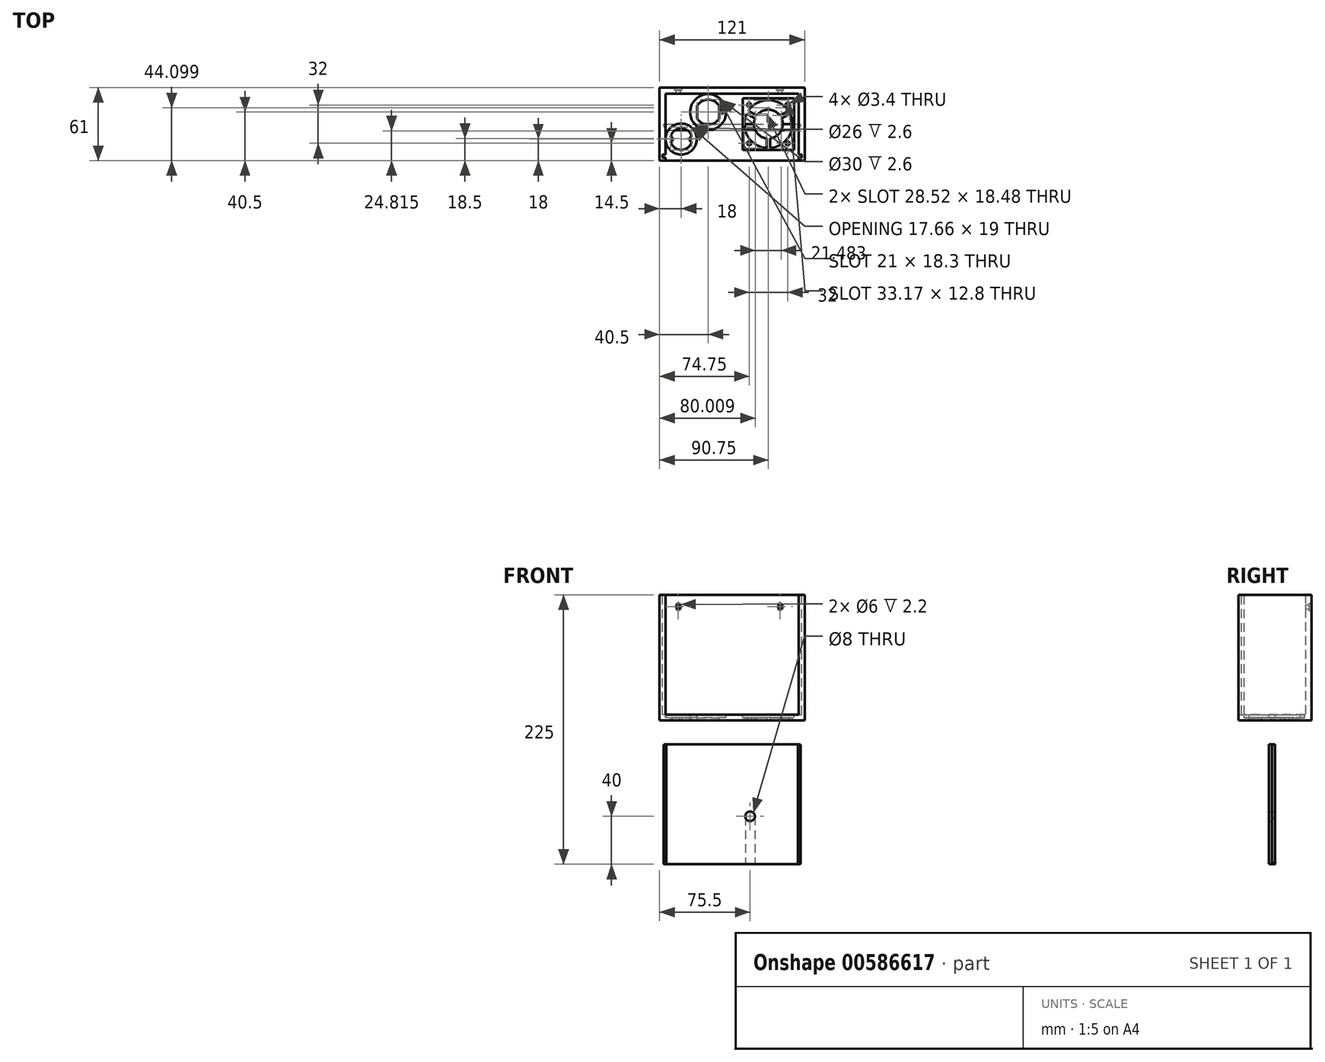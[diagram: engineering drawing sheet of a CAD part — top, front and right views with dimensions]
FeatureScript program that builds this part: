
annotation { "Feature Type Name" : "Feature", "Feature Type Description" : "" }
export const myFeature = defineFeature(function(context is Context, id is Id, definition is map)
    precondition{}
    {
        {
            var Q0;
            Q0=qCreatedBy(makeId("Top.planeOp"),FACE);
            var sketch = newSketch(context, id + "F0", { "sketchPlane" : qUnion([Q0])});
            skLineSegment(sketch, "E0.bottom", {"start": v(-55.5, -25.5) * mm, "end": v(55.5, -25.5) * mm});
            skLineSegment(sketch, "E0.top", {"start": v(-55.5, 25.5) * mm, "end": v(55.5, 25.5) * mm});
            skLineSegment(sketch, "E0.left", {"start": v(-55.5, -25.5) * mm, "end": v(-55.5, 25.5) * mm});
            skLineSegment(sketch, "E0.right", {"start": v(55.5, -25.5) * mm, "end": v(55.5, 25.5) * mm});
            skPoint(sketch, "E0.middle", {"position": v(0, 0) * mm});
            skLineSegment(sketch, "E1.0", {"start": v(60.5, -30.5) * mm, "end": v(60.5, 30.5) * mm});
            skLineSegment(sketch, "E1.1", {"start": v(-60.5, -30.5) * mm, "end": v(60.5, -30.5) * mm});
            skLineSegment(sketch, "E1.2", {"start": v(-60.5, -30.5) * mm, "end": v(-60.5, 30.5) * mm});
            skLineSegment(sketch, "E1.3", {"start": v(-60.5, 30.5) * mm, "end": v(60.5, 30.5) * mm});
            skSolve(sketch);
        }
        {
            var Q0;
            Q0=makeQuery(id+"F0.imprint","IMPRINT",FACE,{"disambiguationData":[TD([[makeQuery(id+"F0.imprint","IMPRINT",EDGE,{"derivedFrom":sQuery(id+"F0.wireOp",EDGE,"E0.bottom")}),-1.0]])]});
            extrude(context, id + "F1", {"entities" : qUnion([Q0]), "depth" : 100 * mm, "offsetDistance" : 25 * mm});
        }
        {
            var Q0;
            Q0=qCreatedBy(makeId("Top.planeOp"),FACE);
            var sketch = newSketch(context, id + "F2", { "sketchPlane" : qUnion([Q0])});
            skLineSegment(sketch, "E2.bottom", {"start": v(60.5, -30.5) * mm, "end": v(-60.5, -30.5) * mm});
            skLineSegment(sketch, "E2.top", {"start": v(60.5, 30.5) * mm, "end": v(-60.5, 30.5) * mm});
            skLineSegment(sketch, "E2.left", {"start": v(60.5, -30.5) * mm, "end": v(60.5, 30.5) * mm});
            skLineSegment(sketch, "E2.right", {"start": v(-60.5, -30.5) * mm, "end": v(-60.5, 30.5) * mm});
            skPoint(sketch, "E2.middle", {"position": v(0, 0) * mm});
            skSolve(sketch);
        }
        {
            var Q0;
            Q0=makeQuery(id+"F2.imprint","IMPRINT",FACE,{"disambiguationData":[TD([[makeQuery(id+"F2.imprint","IMPRINT",EDGE,{"derivedFrom":sQuery(id+"F2.wireOp",EDGE,"E2.bottom")}),-1.0]])]});
            extrude(context, id + "F3", {"entities" : qUnion([Q0]), "operationType" : NewBodyOperationType.ADD, "oppositeDirection" : true, "depth" : 5 * mm, "offsetDistance" : 25 * mm});
        }
        {
            var Q0;
            Q0=qCreatedBy(makeId("Top.planeOp"),FACE);
            var sketch = newSketch(context, id + "F4", { "sketchPlane" : qUnion([Q0])});
            skArc(sketch, "E3", {"start": v(-33.67, -10.75) * mm, "mid": v(-36.41, -5.87) * mm, "end": v(-41.5, -3.56) * mm});
            skArc(sketch, "E4", {"start": v(-29.15, 4.85) * mm, "mid": v(-20, -0.5) * mm, "end": v(-10.85, 4.85) * mm});
            skLineSegment(sketch, "E5.top", {"start": v(-29.15, 15.15) * mm, "end": v(-10.85, 15.15) * mm, "construction": true});
            skLineSegment(sketch, "E5.left", {"start": v(-29.15, 4.85) * mm, "end": v(-29.15, 15.15) * mm});
            skLineSegment(sketch, "E5.right", {"start": v(-10.85, 4.85) * mm, "end": v(-10.85, 15.15) * mm});
            skArc(sketch, "E6.trimOffspring", {"start": v(-10.85, 15.15) * mm, "mid": v(-20, 20.5) * mm, "end": v(-29.15, 15.15) * mm});
            skLineSegment(sketch, "E7.bottom", {"start": v(-35.15, -14.25) * mm, "end": v(-49.85, -14.25) * mm, "construction": true});
            skLineSegment(sketch, "E7.top", {"start": v(-35.15, -10.75) * mm, "end": v(-49.85, -10.75) * mm, "construction": true});
            skLineSegment(sketch, "E7.left", {"start": v(-35.15, -14.25) * mm, "end": v(-35.15, -10.75) * mm});
            skLineSegment(sketch, "E7.right", {"start": v(-49.85, -14.25) * mm, "end": v(-49.85, -10.75) * mm});
            skLineSegment(sketch, "E8", {"start": v(-49.85, -14.25) * mm, "end": v(-51.33, -14.25) * mm});
            skLineSegment(sketch, "E9", {"start": v(-35.15, -10.75) * mm, "end": v(-33.67, -10.75) * mm});
            skLineSegment(sketch, "E10", {"start": v(-35.15, -14.25) * mm, "end": v(-33.67, -14.25) * mm});
            skLineSegment(sketch, "E11", {"start": v(-49.85, -10.75) * mm, "end": v(-51.33, -10.75) * mm});
            skArc(sketch, "E12.trimOffspring", {"start": v(-51.33, -14.25) * mm, "mid": v(-42.5, -21.5) * mm, "end": v(-33.67, -14.25) * mm});
            skArc(sketch, "E13", {"start": v(-41.5, -3.56) * mm, "mid": v(-42.5, -2.5) * mm, "end": v(-43.5, -3.56) * mm});
            skArc(sketch, "E14.trimOffspring", {"start": v(-43.5, -3.56) * mm, "mid": v(-48.59, -5.87) * mm, "end": v(-51.33, -10.75) * mm});
            skSolve(sketch);
        }
        {
            var Q0;
            Q0=makeQuery(id+"F4.imprint","IMPRINT",FACE,{"disambiguationData":[TD([[makeQuery(id+"F4.imprint","IMPRINT",EDGE,{"derivedFrom":sQuery(id+"F4.wireOp",EDGE,"E3")}),1.0]])]});
            var Q1;
            Q1=makeQuery(id+"F4.imprint","IMPRINT",FACE,{"disambiguationData":[TD([[makeQuery(id+"F4.imprint","IMPRINT",EDGE,{"derivedFrom":sQuery(id+"F4.wireOp",EDGE,"E4")}),1.0]])]});
            var Q2;
            Q2=sQuery(id+"F4.wireOp",EDGE,"E3");
            extrude(context, id + "F5", {"entities" : qUnion([Q0, Q1]), "operationType" : NewBodyOperationType.REMOVE, "surfaceEntities" : qUnion([Q2]), "oppositeDirection" : true, "depth" : 25 * mm, "offsetDistance" : 25 * mm});
        }
        {
            var Q0;
            Q0=makeQuery(id+"F3.boolean.opBoolean","MERGE",FACE,{"derivedFrom":[makeQuery(id+"F1.opExtrude","SWEPT_FACE",FACE,{"disambiguationData":[OSD([sQuery(id+"F0.wireOp",EDGE,"E1.3")])]}),makeQuery(id+"F3.opExtrude","SWEPT_FACE",FACE,{"disambiguationData":[OSD([sQuery(id+"F2.wireOp",EDGE,"E2.top")])]})]});
            cPlane(context, id + "F6", {"entities" : qUnion([Q0]), "cplaneType" : CPlaneType.OFFSET, "offset" : 0 * mm, "width" : 150 * mm, "height" : 150 * mm});
        }
        {
            var Q0;
            Q0=qCreatedBy(id+"F6.planeOp",FACE);
            var sketch = newSketch(context, id + "F7", { "sketchPlane" : qUnion([Q0])});
            skCircle(sketch, "E15", {"center": v(45, 90) * mm, "radius": 1.7 * mm});
            skLineSegment(sketch, "E16.bottom", {"start": v(-55.5, 0) * mm, "end": v(55.5, 0) * mm});
            skLineSegment(sketch, "E16.top", {"start": v(-55.5, 100) * mm, "end": v(55.5, 100) * mm});
            skLineSegment(sketch, "E16.left", {"start": v(-55.5, 0) * mm, "end": v(-55.5, 100) * mm});
            skLineSegment(sketch, "E16.right", {"start": v(55.5, 0) * mm, "end": v(55.5, 100) * mm});
            skCircle(sketch, "E17", {"center": v(-40, 90) * mm, "radius": 1.7 * mm});
            skSolve(sketch);
        }
        {
            var Q0;
            Q0=makeQuery(id+"F7.imprint","IMPRINT",FACE,{"disambiguationData":[TD([[makeQuery(id+"F7.imprint","IMPRINT",EDGE,{"derivedFrom":sQuery(id+"F7.wireOp",EDGE,"E17")}),1.0]])]});
            var Q1;
            Q1=makeQuery(id+"F7.imprint","IMPRINT",FACE,{"disambiguationData":[TD([[makeQuery(id+"F7.imprint","IMPRINT",EDGE,{"derivedFrom":sQuery(id+"F7.wireOp",EDGE,"E15")}),1.0]])]});
            extrude(context, id + "F8", {"entities" : qUnion([Q0, Q1]), "operationType" : NewBodyOperationType.REMOVE, "oppositeDirection" : true, "depth" : 25 * mm, "offsetDistance" : 25 * mm});
        }
        {
            var Q0;
            Q0=makeQuery(id+"F3.opExtrude","CAP_FACE",FACE,{"disambiguationData":[OSD([sQuery(id+"F2.wireOp",EDGE,"E2.bottom"),sQuery(id+"F2.wireOp",EDGE,"E2.top"),sQuery(id+"F2.wireOp",EDGE,"E2.left"),sQuery(id+"F2.wireOp",EDGE,"E2.right")])],"isStart":false});
            cPlane(context, id + "F9", {"entities" : qUnion([Q0]), "cplaneType" : CPlaneType.OFFSET, "offset" : 0 * mm, "width" : 150 * mm, "height" : 150 * mm});
        }
        {
            var Q0;
            Q0=qCreatedBy(id+"F9.planeOp",FACE);
            var sketch = newSketch(context, id + "F10", { "sketchPlane" : qUnion([Q0])});
            skLineSegment(sketch, "E18.bottom", {"start": v(46.25, 16) * mm, "end": v(14.25, 16) * mm, "construction": true});
            skLineSegment(sketch, "E18.top", {"start": v(46.25, -16) * mm, "end": v(14.25, -16) * mm, "construction": true});
            skLineSegment(sketch, "E18.left", {"start": v(46.25, 16) * mm, "end": v(46.25, -16) * mm, "construction": true});
            skLineSegment(sketch, "E18.right", {"start": v(14.25, 16) * mm, "end": v(14.25, -16) * mm, "construction": true});
            skPoint(sketch, "E18.middle", {"position": v(30.25, 0) * mm});
            skLineSegment(sketch, "E19", {"start": v(0, 0) * mm, "end": v(60.5, 0) * mm, "construction": true});
            skCircle(sketch, "E20", {"center": v(14.25, 16) * mm, "radius": 1.7 * mm});
            skCircle(sketch, "E21", {"center": v(46.25, 16) * mm, "radius": 1.7 * mm});
            skCircle(sketch, "E22", {"center": v(46.25, -16) * mm, "radius": 1.7 * mm});
            skCircle(sketch, "E23", {"center": v(14.25, -16) * mm, "radius": 1.7 * mm});
            skLineSegment(sketch, "E24.bottom", {"start": v(30.25, 20) * mm, "end": v(50.25, 20) * mm, "construction": true});
            skLineSegment(sketch, "E24.top", {"start": v(10.25, -20) * mm, "end": v(50.25, -20) * mm, "construction": true});
            skLineSegment(sketch, "E24.left", {"start": v(10.25, 20) * mm, "end": v(10.25, -20) * mm, "construction": true});
            skLineSegment(sketch, "E24.right", {"start": v(50.25, 20) * mm, "end": v(50.25, -20) * mm, "construction": true});
            skArc(sketch, "E25", {"start": v(28.75, 19.94) * mm, "mid": v(12.96, 10.05) * mm, "end": v(12.18, -8.57) * mm});
            skArc(sketch, "E26", {"start": v(28.75, 11.9) * mm, "mid": v(19.87, 6.03) * mm, "end": v(19.16, -4.6) * mm});
            skLineSegment(sketch, "E27", {"start": v(30.25, 0) * mm, "end": v(30.25, 20) * mm, "construction": true});
            skLineSegment(sketch, "E28", {"start": v(30.25, 0) * mm, "end": v(47.63, -9.9) * mm, "construction": true});
            skLineSegment(sketch, "E29.MirrorCS", {"start": v(30.25, 0) * mm, "end": v(12.87, -9.9) * mm, "construction": true});
            skLineSegment(sketch, "E30.0", {"start": v(31.75, 11.9) * mm, "end": v(31.75, 19.94) * mm});
            skLineSegment(sketch, "E30.1", {"start": v(41.34, -4.6) * mm, "end": v(48.32, -8.57) * mm});
            skLineSegment(sketch, "E31.0", {"start": v(39.85, -7.2) * mm, "end": v(46.83, -11.18) * mm});
            skLineSegment(sketch, "E31.1", {"start": v(20.65, -7.2) * mm, "end": v(13.67, -11.18) * mm});
            skLineSegment(sketch, "E32.1", {"start": v(28.75, 11.9) * mm, "end": v(28.75, 19.94) * mm});
            skPoint(sketch, "E33.orphan", {"position": v(10.25, -11.4) * mm});
            skPoint(sketch, "E34.orphan", {"position": v(50.25, -11.4) * mm});
            skLineSegment(sketch, "E35.trimOffspring", {"start": v(19.16, -4.6) * mm, "end": v(12.18, -8.57) * mm});
            skArc(sketch, "E36.trimOffspring", {"start": v(41.34, -4.6) * mm, "mid": v(40.63, 6.03) * mm, "end": v(31.75, 11.9) * mm});
            skArc(sketch, "E37.trimOffspring", {"start": v(48.32, -8.57) * mm, "mid": v(47.54, 10.05) * mm, "end": v(31.75, 19.94) * mm});
            skArc(sketch, "E38.trimOffspring", {"start": v(20.65, -7.2) * mm, "mid": v(30.25, -12) * mm, "end": v(39.85, -7.2) * mm});
            skArc(sketch, "E39.trimOffspring", {"start": v(13.67, -11.18) * mm, "mid": v(30.25, -20) * mm, "end": v(46.83, -11.18) * mm});
            skSolve(sketch);
        }
        {
            var Q0;
            Q0=makeQuery(id+"F10.imprint","IMPRINT",FACE,{"disambiguationData":[TD([[makeQuery(id+"F10.imprint","IMPRINT",EDGE,{"derivedFrom":sQuery(id+"F10.wireOp",EDGE,"E20")}),1.0]])]});
            var Q1;
            Q1=makeQuery(id+"F10.imprint","IMPRINT",FACE,{"disambiguationData":[TD([[makeQuery(id+"F10.imprint","IMPRINT",EDGE,{"derivedFrom":sQuery(id+"F10.wireOp",EDGE,"E25")}),1.0]])]});
            var Q2;
            Q2=makeQuery(id+"F10.imprint","IMPRINT",FACE,{"disambiguationData":[TD([[makeQuery(id+"F10.imprint","IMPRINT",EDGE,{"derivedFrom":sQuery(id+"F10.wireOp",EDGE,"E30.0")}),-1.0]])]});
            var Q3;
            Q3=makeQuery(id+"F10.imprint","IMPRINT",FACE,{"disambiguationData":[TD([[makeQuery(id+"F10.imprint","IMPRINT",EDGE,{"derivedFrom":sQuery(id+"F10.wireOp",EDGE,"E21")}),1.0]])]});
            var Q4;
            Q4=makeQuery(id+"F10.imprint","IMPRINT",FACE,{"disambiguationData":[TD([[makeQuery(id+"F10.imprint","IMPRINT",EDGE,{"derivedFrom":sQuery(id+"F10.wireOp",EDGE,"E31.0")}),-1.0]])]});
            var Q5;
            Q5=makeQuery(id+"F10.imprint","IMPRINT",FACE,{"disambiguationData":[TD([[makeQuery(id+"F10.imprint","IMPRINT",EDGE,{"derivedFrom":sQuery(id+"F10.wireOp",EDGE,"E23")}),1.0]])]});
            var Q6;
            Q6=makeQuery(id+"F10.imprint","IMPRINT",FACE,{"disambiguationData":[TD([[makeQuery(id+"F10.imprint","IMPRINT",EDGE,{"derivedFrom":sQuery(id+"F10.wireOp",EDGE,"E22")}),1.0]])]});
            extrude(context, id + "F11", {"entities" : qUnion([Q0, Q1, Q2, Q3, Q4, Q5, Q6]), "operationType" : NewBodyOperationType.REMOVE, "oppositeDirection" : true, "depth" : 25 * mm, "offsetDistance" : 25 * mm});
        }
        {
            var Q0;
            Q0=qCreatedBy(id+"F6.planeOp",FACE);
            var sketch = newSketch(context, id + "F12", { "sketchPlane" : qUnion([Q0])});
            skCircle(sketch, "E40", {"center": v(-40, 90) * mm, "radius": 3 * mm});
            skCircle(sketch, "E41", {"center": v(45, 90) * mm, "radius": 3 * mm});
            skSolve(sketch);
        }
        {
            var Q0;
            Q0=makeQuery(id+"F12.imprint","IMPRINT",FACE,{"disambiguationData":[TD([[makeQuery(id+"F12.imprint","IMPRINT",EDGE,{"derivedFrom":sQuery(id+"F12.wireOp",EDGE,"E40")}),1.0]])]});
            var Q1;
            Q1=makeQuery(id+"F12.imprint","IMPRINT",FACE,{"disambiguationData":[TD([[makeQuery(id+"F12.imprint","IMPRINT",EDGE,{"derivedFrom":sQuery(id+"F12.wireOp",EDGE,"E41")}),1.0]])]});
            extrude(context, id + "F13", {"entities" : qUnion([Q0, Q1]), "operationType" : NewBodyOperationType.REMOVE, "oppositeDirection" : true, "depth" : 2.2 * mm, "offsetDistance" : 25 * mm});
        }
        {
            var Q0;
            Q0=qCreatedBy(makeId("Top.planeOp"),FACE);
            var sketch = newSketch(context, id + "F14", { "sketchPlane" : qUnion([Q0])});
            skCircle(sketch, "E42", {"center": v(-20, 10) * mm, "radius": 15 * mm});
            skCircle(sketch, "E43", {"center": v(-42.5, -12.5) * mm, "radius": 13 * mm});
            skLineSegment(sketch, "E44.bottom", {"start": v(8.75, -21.5) * mm, "end": v(51.75, -21.5) * mm});
            skLineSegment(sketch, "E44.top", {"start": v(8.75, 21.5) * mm, "end": v(51.75, 21.5) * mm});
            skLineSegment(sketch, "E44.left", {"start": v(8.75, -21.5) * mm, "end": v(8.75, 21.5) * mm});
            skLineSegment(sketch, "E44.right", {"start": v(51.75, -21.5) * mm, "end": v(51.75, 21.5) * mm});
            skPoint(sketch, "E44.middle", {"position": v(30.25, 0) * mm});
            skSolve(sketch);
        }
        {
            var Q0;
            Q0=makeQuery(id+"F14.imprint","IMPRINT",FACE,{"disambiguationData":[TD([[makeQuery(id+"F14.imprint","IMPRINT",EDGE,{"derivedFrom":sQuery(id+"F14.wireOp",EDGE,"E42")}),1.0]])]});
            var Q1;
            Q1=makeQuery(id+"F14.imprint","IMPRINT",FACE,{"disambiguationData":[TD([[makeQuery(id+"F14.imprint","IMPRINT",EDGE,{"derivedFrom":sQuery(id+"F14.wireOp",EDGE,"E43")}),1.0]])]});
            var Q2;
            Q2=makeQuery(id+"F14.imprint","IMPRINT",FACE,{"disambiguationData":[TD([[makeQuery(id+"F14.imprint","IMPRINT",EDGE,{"derivedFrom":sQuery(id+"F14.wireOp",EDGE,"E44.bottom")}),1.0]])]});
            extrude(context, id + "F15", {"entities" : qUnion([Q0, Q1, Q2]), "operationType" : NewBodyOperationType.REMOVE, "oppositeDirection" : true, "depth" : 2.6 * mm, "offsetDistance" : 25 * mm});
        }
        {
            var Q0;
            Q0=makeQuery(id+"F3.boolean.opBoolean","MERGE",FACE,{"derivedFrom":[makeQuery(id+"F1.opExtrude","SWEPT_FACE",FACE,{"disambiguationData":[OSD([sQuery(id+"F0.wireOp",EDGE,"E1.1")])]}),makeQuery(id+"F3.opExtrude","SWEPT_FACE",FACE,{"disambiguationData":[OSD([sQuery(id+"F2.wireOp",EDGE,"E2.bottom")])]})]});
            cPlane(context, id + "F16", {"entities" : qUnion([Q0]), "cplaneType" : CPlaneType.OFFSET, "offset" : 0 * mm, "width" : 150 * mm, "height" : 150 * mm});
        }
        {
            var Q0;
            Q0=qCreatedBy(id+"F16.planeOp",FACE);
            var sketch = newSketch(context, id + "F17", { "sketchPlane" : qUnion([Q0])});
            skLineSegment(sketch, "E45.bottom", {"start": v(-55.5, 100) * mm, "end": v(55.5, 100) * mm});
            skLineSegment(sketch, "E45.top", {"start": v(-55.5, 0) * mm, "end": v(55.5, 0) * mm});
            skLineSegment(sketch, "E45.left", {"start": v(-55.5, 100) * mm, "end": v(-55.5, 0) * mm});
            skLineSegment(sketch, "E45.right", {"start": v(55.5, 100) * mm, "end": v(55.5, 0) * mm});
            skSolve(sketch);
        }
        {
            var Q0;
            Q0 = qSketchRegion(id + "F17", true);
            extrude(context, id + "F18", {"entities" : qUnion([Q0]), "operationType" : NewBodyOperationType.REMOVE, "oppositeDirection" : true, "depth" : 25 * mm, "offsetDistance" : 25 * mm});
        }
        {
            var Q0;
            Q0=makeQuery(id+"F1.opExtrude","CAP_FACE",FACE,{"disambiguationData":[OSD([sQuery(id+"F0.wireOp",EDGE,"E0.bottom"),sQuery(id+"F0.wireOp",EDGE,"E0.top"),sQuery(id+"F0.wireOp",EDGE,"E0.left"),sQuery(id+"F0.wireOp",EDGE,"E0.right"),sQuery(id+"F0.wireOp",EDGE,"E1.0"),sQuery(id+"F0.wireOp",EDGE,"E1.1"),sQuery(id+"F0.wireOp",EDGE,"E1.2"),sQuery(id+"F0.wireOp",EDGE,"E1.3")])],"isStart":false});
            cPlane(context, id + "F19", {"entities" : qUnion([Q0]), "cplaneType" : CPlaneType.OFFSET, "offset" : 0 * mm, "width" : 150 * mm, "height" : 150 * mm});
        }
        {
            var Q0;
            Q0=qCreatedBy(id+"F19.planeOp",FACE);
            var sketch = newSketch(context, id + "F20", { "sketchPlane" : qUnion([Q0])});
            skLineSegment(sketch, "E46.bottom", {"start": v(55.5, -28) * mm, "end": v(58, -28) * mm});
            skLineSegment(sketch, "E46.top", {"start": v(55.5, -25.5) * mm, "end": v(58, -25.5) * mm});
            skLineSegment(sketch, "E46.left", {"start": v(55.5, -28) * mm, "end": v(55.5, -25.5) * mm});
            skLineSegment(sketch, "E46.right", {"start": v(58, -28) * mm, "end": v(58, -25.5) * mm});
            skLineSegment(sketch, "E47.MirrorCS", {"start": v(-55.5, -25.5) * mm, "end": v(-58, -25.5) * mm});
            skLineSegment(sketch, "E48.MirrorCS", {"start": v(-58, -28) * mm, "end": v(-58, -25.5) * mm});
            skLineSegment(sketch, "E49.MirrorCS", {"start": v(-55.5, -28) * mm, "end": v(-58, -28) * mm});
            skLineSegment(sketch, "E50.MirrorCS", {"start": v(-55.5, -28) * mm, "end": v(-55.5, -25.5) * mm});
            skSolve(sketch);
        }
        {
            var Q0;
            Q0=makeQuery(id+"F20.imprint","IMPRINT",FACE,{"disambiguationData":[TD([[makeQuery(id+"F20.imprint","IMPRINT",EDGE,{"derivedFrom":sQuery(id+"F20.wireOp",EDGE,"E47.MirrorCS")}),1.0]])]});
            var Q1;
            Q1=makeQuery(id+"F20.imprint","IMPRINT",FACE,{"disambiguationData":[TD([[makeQuery(id+"F20.imprint","IMPRINT",EDGE,{"derivedFrom":sQuery(id+"F20.wireOp",EDGE,"E46.bottom")}),1.0]])]});
            extrude(context, id + "F21", {"entities" : qUnion([Q0, Q1]), "operationType" : NewBodyOperationType.REMOVE, "oppositeDirection" : true, "depth" : 100 * mm, "offsetDistance" : 25 * mm});
        }
        {
            var Q0;
            Q0=qCreatedBy(makeId("Front.planeOp"),FACE);
            var sketch = newSketch(context, id + "F22", { "sketchPlane" : qUnion([Q0])});
            skLineSegment(sketch, "E51.bottom", {"start": v(-55, -25) * mm, "end": v(55, -25) * mm});
            skLineSegment(sketch, "E51.top", {"start": v(-55, -125) * mm, "end": v(55, -125) * mm});
            skLineSegment(sketch, "E51.left", {"start": v(-55, -25) * mm, "end": v(-55, -125) * mm});
            skLineSegment(sketch, "E51.right", {"start": v(55, -25) * mm, "end": v(55, -125) * mm});
            skPoint(sketch, "E51.middle", {"position": v(0, -75) * mm});
            skLineSegment(sketch, "E52", {"start": v(0, 0) * mm, "end": v(0, -150) * mm, "construction": true});
            skCircle(sketch, "E53", {"center": v(15, -85) * mm, "radius": 4 * mm});
            skSolve(sketch);
        }
        {
            var Q0;
            Q0=makeQuery(id+"F22.imprint","IMPRINT",FACE,{"disambiguationData":[TD([[makeQuery(id+"F22.imprint","IMPRINT",EDGE,{"derivedFrom":sQuery(id+"F22.wireOp",EDGE,"E51.bottom")}),-1.0]])]});
            extrude(context, id + "F23", {"entities" : qUnion([Q0]), "depth" : 5 * mm, "offsetDistance" : 25 * mm});
        }
        {
            var Q0;
            Q0=makeQuery(id+"F23.opExtrude","SWEPT_FACE",FACE,{"disambiguationData":[OSD([sQuery(id+"F22.wireOp",EDGE,"E51.top")])]});
            var sketch = newSketch(context, id + "F24", { "sketchPlane" : qUnion([Q0])});
            skLineSegment(sketch, "E54.bottom", {"start": v(55, 0) * mm, "end": v(57.3, 0) * mm});
            skLineSegment(sketch, "E54.top", {"start": v(55, 2.3) * mm, "end": v(57.3, 2.3) * mm});
            skLineSegment(sketch, "E54.left", {"start": v(55, 0) * mm, "end": v(55, 2.3) * mm});
            skLineSegment(sketch, "E54.right", {"start": v(57.3, 0) * mm, "end": v(57.3, 2.3) * mm});
            skLineSegment(sketch, "E55.MirrorCS", {"start": v(-55, 0) * mm, "end": v(-55, 2.3) * mm});
            skLineSegment(sketch, "E56.MirrorCS", {"start": v(-55, 2.3) * mm, "end": v(-57.3, 2.3) * mm});
            skLineSegment(sketch, "E57.MirrorCS", {"start": v(-57.3, 0) * mm, "end": v(-57.3, 2.3) * mm});
            skLineSegment(sketch, "E58.MirrorCS", {"start": v(-55, 0) * mm, "end": v(-57.3, 0) * mm});
            skSolve(sketch);
        }
        {
            var Q0;
            Q0=makeQuery(id+"F24.imprint","IMPRINT",FACE,{"disambiguationData":[TD([[makeQuery(id+"F24.imprint","IMPRINT",EDGE,{"derivedFrom":sQuery(id+"F24.wireOp",EDGE,"E54.bottom")}),1.0]])]});
            var Q1;
            Q1=makeQuery(id+"F24.imprint","IMPRINT",FACE,{"disambiguationData":[TD([[makeQuery(id+"F24.imprint","IMPRINT",EDGE,{"derivedFrom":sQuery(id+"F24.wireOp",EDGE,"E55.MirrorCS")}),-1.0]])]});
            extrude(context, id + "F25", {"entities" : qUnion([Q0, Q1]), "operationType" : NewBodyOperationType.ADD, "oppositeDirection" : true, "depth" : 100 * mm, "offsetDistance" : 25 * mm});
        }
        {
            var Q0;
            Q0=makeQuery(id+"F25.opExtrude","SWEPT_FACE",FACE,{"disambiguationData":[OSD([sQuery(id+"F24.wireOp",EDGE,"E54.right")])]});
            var Q1;
            Q1=makeQuery(id+"F25.opExtrude","SWEPT_FACE",FACE,{"disambiguationData":[OSD([sQuery(id+"F24.wireOp",EDGE,"E57.MirrorCS")])]});
            fillet(context, id + "F26", {"entities" : qUnion([Q0, Q1]), "radius" : 1 * mm, "tangentPropagation" : true, "allowEdgeOverflow" : false});
        }
        {
            var Q0;
            Q0=makeQuery(id+"F25.boolean.opBoolean","MERGE",FACE,{"derivedFrom":[makeQuery(id+"F23.opExtrude","SWEPT_FACE",FACE,{"disambiguationData":[OSD([sQuery(id+"F22.wireOp",EDGE,"E51.top")])]}),makeQuery(id+"F25.opExtrude","CAP_FACE",FACE,{"disambiguationData":[OSD([sQuery(id+"F24.wireOp",EDGE,"E54.bottom"),sQuery(id+"F24.wireOp",EDGE,"E54.top"),sQuery(id+"F24.wireOp",EDGE,"E54.left"),sQuery(id+"F24.wireOp",EDGE,"E54.right")])],"isStart":true}),makeQuery(id+"F25.opExtrude","CAP_FACE",FACE,{"disambiguationData":[OSD([sQuery(id+"F24.wireOp",EDGE,"E55.MirrorCS"),sQuery(id+"F24.wireOp",EDGE,"E56.MirrorCS"),sQuery(id+"F24.wireOp",EDGE,"E57.MirrorCS"),sQuery(id+"F24.wireOp",EDGE,"E58.MirrorCS")])],"isStart":true})]});
            cPlane(context, id + "F27", {"entities" : qUnion([Q0]), "cplaneType" : CPlaneType.OFFSET, "offset" : 0 * mm, "width" : 150 * mm, "height" : 150 * mm});
        }
        {
            var Q0;
            Q0=qCreatedBy(id+"F27.planeOp",FACE);
            var sketch = newSketch(context, id + "F28", { "sketchPlane" : qUnion([Q0])});
            skLineSegment(sketch, "E59.bottom", {"start": v(11, 0) * mm, "end": v(19, 0) * mm});
            skLineSegment(sketch, "E59.top", {"start": v(11, 2.6) * mm, "end": v(19, 2.6) * mm});
            skLineSegment(sketch, "E59.left", {"start": v(11, 0) * mm, "end": v(11, 2.6) * mm});
            skLineSegment(sketch, "E59.right", {"start": v(19, 0) * mm, "end": v(19, 2.6) * mm});
            skLineSegment(sketch, "E60", {"start": v(15, 2.6) * mm, "end": v(15, 0) * mm, "construction": true});
            skSolve(sketch);
        }
        {
            var Q0;
            Q0=makeQuery(id+"F28.imprint","IMPRINT",FACE,{"disambiguationData":[TD([[makeQuery(id+"F28.imprint","IMPRINT",EDGE,{"derivedFrom":sQuery(id+"F28.wireOp",EDGE,"E59.bottom")}),1.0]])]});
            extrude(context, id + "F29", {"entities" : qUnion([Q0]), "operationType" : NewBodyOperationType.REMOVE, "endBound" : BoundingType.UP_TO_NEXT, "oppositeDirection" : true, "depth" : 1 * mm, "offsetDistance" : 25 * mm});
        }
        {
            var Q0;
            Q0=makeQuery(id+"F29.boolean.opBoolean","COPY",EDGE,{"derivedFrom":makeQuery(id+"F29.opExtrude","SWEPT_EDGE",EDGE,{"disambiguationData":[OSD([sQuery(id+"F28.wireOp",EDGE,"E59.top"),sQuery(id+"F28.wireOp",EDGE,"E59.right")])]})});
            var Q1;
            Q1=makeQuery(id+"F29.boolean.opBoolean","COPY",EDGE,{"derivedFrom":makeQuery(id+"F29.opExtrude","SWEPT_EDGE",EDGE,{"disambiguationData":[OSD([sQuery(id+"F28.wireOp",EDGE,"E59.top"),sQuery(id+"F28.wireOp",EDGE,"E59.left")])]})});
            fillet(context, id + "F30", {"entities" : qUnion([Q0, Q1]), "radius" : 2.6 * mm, "tangentPropagation" : true, "allowEdgeOverflow" : false});
        }
    });
